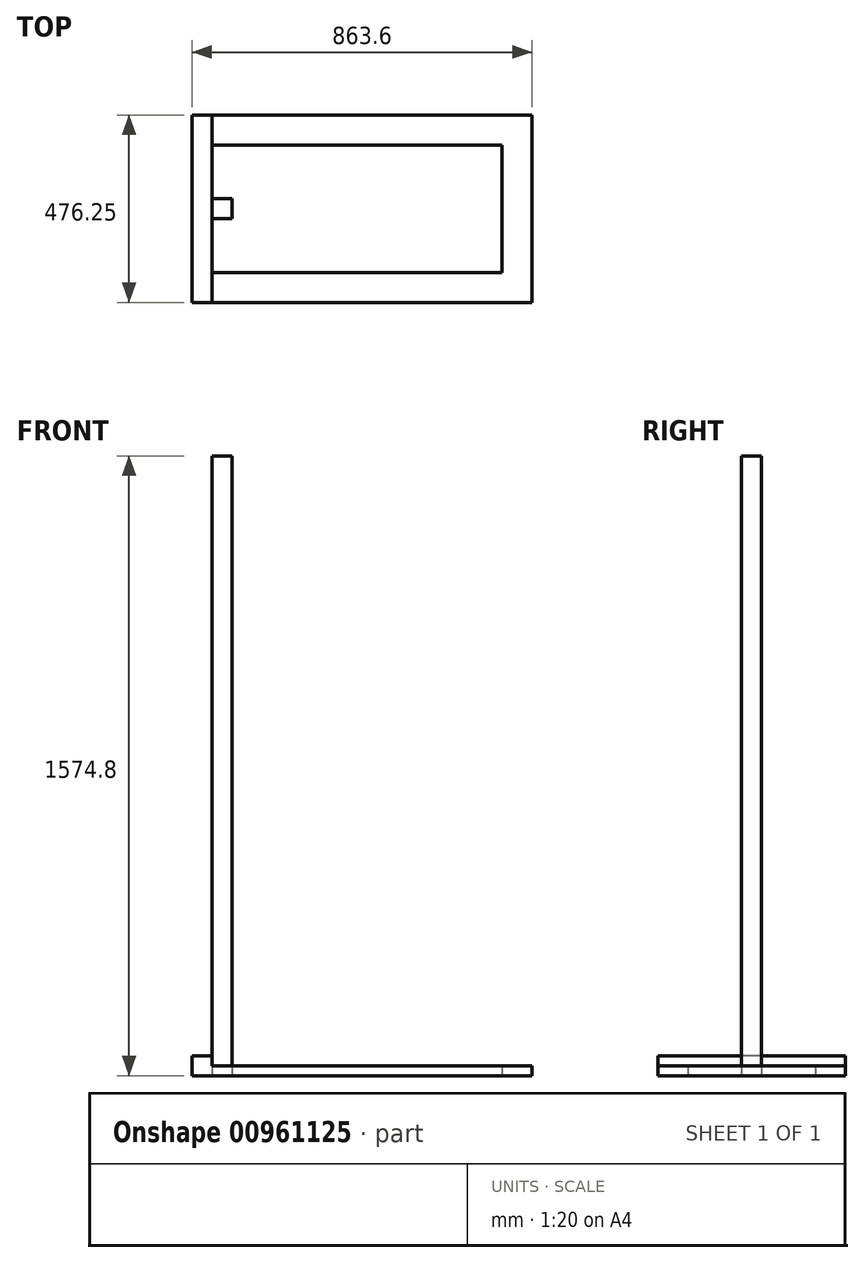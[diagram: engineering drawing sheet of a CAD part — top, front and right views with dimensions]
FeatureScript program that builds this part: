
annotation { "Feature Type Name" : "Feature", "Feature Type Description" : "" }
export const myFeature = defineFeature(function(context is Context, id is Id, definition is map)
    precondition{}
    {
        {
            var Q0;
            Q0=qCreatedBy(makeId("Top.planeOp"),FACE);
            var sketch = newSketch(context, id + "F0", { "sketchPlane" : qUnion([Q0])});
            skLineSegment(sketch, "E0.bottom", {"start": v(0, 157) * mm, "end": v(812.8, 157) * mm});
            skLineSegment(sketch, "E0.top", {"start": v(0, 233.2) * mm, "end": v(812.8, 233.2) * mm});
            skLineSegment(sketch, "E0.left", {"start": v(0, 157) * mm, "end": v(0, 233.2) * mm});
            skLineSegment(sketch, "E0.right", {"start": v(812.8, 157) * mm, "end": v(812.8, 233.2) * mm});
            skLineSegment(sketch, "E1.bottom", {"start": v(0, -166.85) * mm, "end": v(812.8, -166.85) * mm});
            skLineSegment(sketch, "E1.top", {"start": v(0, -243.05) * mm, "end": v(812.8, -243.05) * mm});
            skLineSegment(sketch, "E1.left", {"start": v(0, -166.85) * mm, "end": v(0, -243.05) * mm});
            skLineSegment(sketch, "E1.right", {"start": v(812.8, -166.85) * mm, "end": v(812.8, -243.05) * mm});
            skLineSegment(sketch, "E2.bottom", {"start": v(0, 233.2) * mm, "end": v(-50.8, 233.2) * mm});
            skLineSegment(sketch, "E2.top", {"start": v(0, -243.05) * mm, "end": v(-50.8, -243.05) * mm});
            skLineSegment(sketch, "E2.left", {"start": v(0, 233.2) * mm, "end": v(0, -243.05) * mm});
            skLineSegment(sketch, "E2.right", {"start": v(-50.8, 233.2) * mm, "end": v(-50.8, -243.05) * mm});
            skLineSegment(sketch, "E3.bottom", {"start": v(0, 20.47) * mm, "end": v(50.8, 20.47) * mm});
            skLineSegment(sketch, "E3.top", {"start": v(0, -30.33) * mm, "end": v(50.8, -30.33) * mm});
            skLineSegment(sketch, "E3.left", {"start": v(0, 20.47) * mm, "end": v(0, -30.33) * mm});
            skLineSegment(sketch, "E3.right", {"start": v(50.8, 20.47) * mm, "end": v(50.8, -30.33) * mm});
            skLineSegment(sketch, "E4.bottom", {"start": v(812.8, 157) * mm, "end": v(736.6, 157) * mm});
            skLineSegment(sketch, "E4.top", {"start": v(812.8, -166.85) * mm, "end": v(736.6, -166.85) * mm});
            skLineSegment(sketch, "E4.left", {"start": v(812.8, 157) * mm, "end": v(812.8, -166.85) * mm});
            skLineSegment(sketch, "E4.right", {"start": v(736.6, 157) * mm, "end": v(736.6, -166.85) * mm});
            skSolve(sketch);
        }
        {
            var Q0;
            Q0=makeQuery(id+"F0.imprint","IMPRINT",FACE,{"disambiguationData":[TD([[makeQuery(id+"F0.imprint","IMPRINT",EDGE,{"derivedFrom":sQuery(id+"F0.wireOp",EDGE,"E0.top")}),-1.0]])]});
            var Q1;
            {var subQ0=sQuery(id+"F0.wireOp",EDGE,"E4.left");Q1=makeQuery(id+"F0.imprint","IMPRINT",FACE,{"disambiguationData":[TD([[makeQuery(id+"F0.imprint","IMPRINT",EDGE,{"derivedFrom":subQ0}),-1.0]])]});}
            var Q2;
            Q2=makeQuery(id+"F0.imprint","IMPRINT",FACE,{"disambiguationData":[TD([[makeQuery(id+"F0.imprint","IMPRINT",EDGE,{"derivedFrom":sQuery(id+"F0.wireOp",EDGE,"E1.top")}),1.0]])]});
            extrude(context, id + "F1", {"entities" : qUnion([Q0, Q1, Q2]), "depth" : 25.4 * mm, "offsetDistance" : 25.4 * mm});
        }
        {
            var Q0;
            {var subQ1=sQuery(id+"F0.wireOp",EDGE,"E0.left");Q0=makeQuery(id+"F0.imprint","IMPRINT",FACE,{"disambiguationData":[TD([[makeQuery(id+"F0.imprint","IMPRINT",EDGE,{"derivedFrom":subQ1}),1.0]])]});}
            extrude(context, id + "F2", {"entities" : qUnion([Q0]), "operationType" : NewBodyOperationType.ADD, "depth" : 50.8 * mm, "offsetDistance" : 25.4 * mm});
        }
        {
            var Q0;
            {var subQ2=sQuery(id+"F0.wireOp",EDGE,"E3.bottom");Q0=makeQuery(id+"F0.imprint","IMPRINT",FACE,{"disambiguationData":[TD([[makeQuery(id+"F0.imprint","IMPRINT",EDGE,{"derivedFrom":subQ2}),-1.0]])]});}
            extrude(context, id + "F3", {"entities" : qUnion([Q0]), "operationType" : NewBodyOperationType.ADD, "depth" : 1574.8 * mm, "offsetDistance" : 25.4 * mm});
        }
    });
